# Revit family: WAL_A3-Classic-Horizontal-Slider-1500x1200-SW1512
name_source: partatom
category: Windows
revit_build: Autodesk Revit 2016 (Build: 20150220_1215(x64)
units: mm (PartAtom-declared; Revit-internal decimal feet)

## family parameters
Always vertical = Yes
Cut with Voids When Loaded = No
Host = Wall
Room Calculation Point = No
Shared = No

## types (1)
- 1500 x 1200 SW1512 Classical Horizontal Slider
    Assembly Code = B2020110
    Default Sill Height = 800 mm  [stored 2.62467 ft]
    Description = Classic Horizontal Slider
    Frame Material = Metal Aluminium
    Glass Material = Glass
    Height = 1200 mm
    Manufacturer = AGI Aluminium
    Manufacturer Code = SW1512
    Model = Slider
    URL = www.agi.co.za
    Wall Closure = By host
    Width = 1500 mm  [stored 4.92126 ft]

note: [stored X ft] marks values corroborated as IEEE doubles in the binary element streams (Revit-internal decimal feet)

## geometry (parser evidence)
native form markers: Sweep x10
no freeform markers — native parametric forms only
